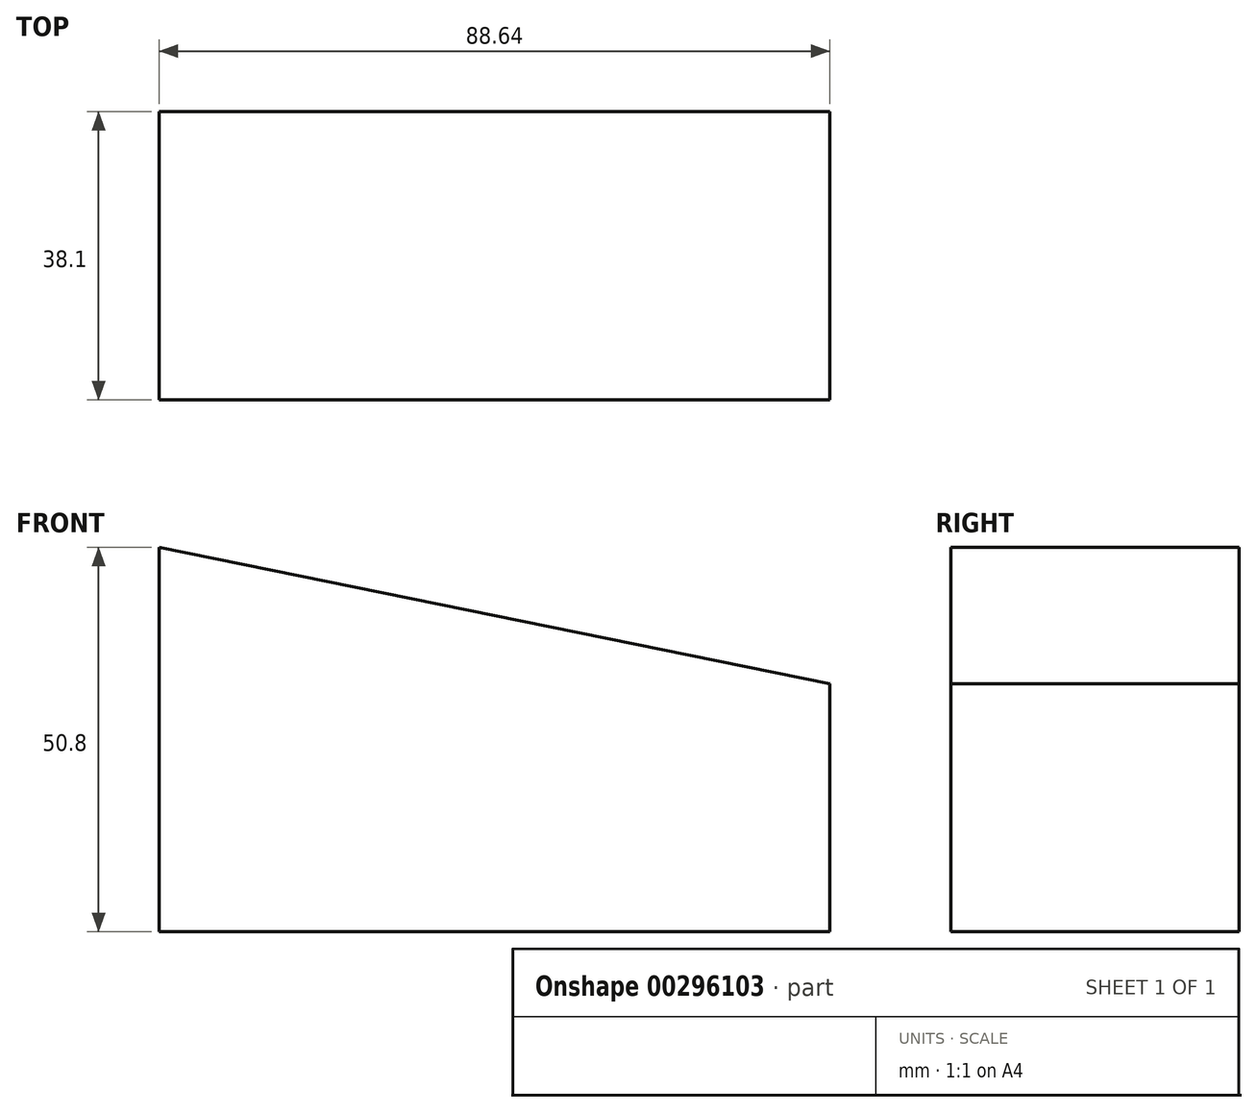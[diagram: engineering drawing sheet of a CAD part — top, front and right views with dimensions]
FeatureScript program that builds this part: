
annotation { "Feature Type Name" : "Feature", "Feature Type Description" : "" }
export const myFeature = defineFeature(function(context is Context, id is Id, definition is map)
    precondition{}
    {
        {
            var Q0;
            Q0=qCreatedBy(makeId("Front.planeOp"),FACE);
            var sketch = newSketch(context, id + "F0", { "sketchPlane" : qUnion([Q0])});
            skLineSegment(sketch, "E0", {"start": v(-38, 40.23) * mm, "end": v(-38, -10.57) * mm});
            skLineSegment(sketch, "E1", {"start": v(-38, -10.57) * mm, "end": v(50.64, -10.57) * mm});
            skLineSegment(sketch, "E2", {"start": v(50.64, -10.57) * mm, "end": v(50.64, 22.2) * mm});
            skLineSegment(sketch, "E3", {"start": v(-38, 40.23) * mm, "end": v(50.64, 22.2) * mm});
            skSolve(sketch);
        }
        {
            var Q0;
            Q0=makeQuery(id+"F0.imprint","IMPRINT",FACE,{"disambiguationData":[TD([[makeQuery(id+"F0.imprint","IMPRINT",EDGE,{"derivedFrom":sQuery(id+"F0.wireOp",EDGE,"E0")}),1.0]])]});
            extrude(context, id + "F1", {"entities" : qUnion([Q0]), "depth" : 38.1 * mm});
        }
    });
